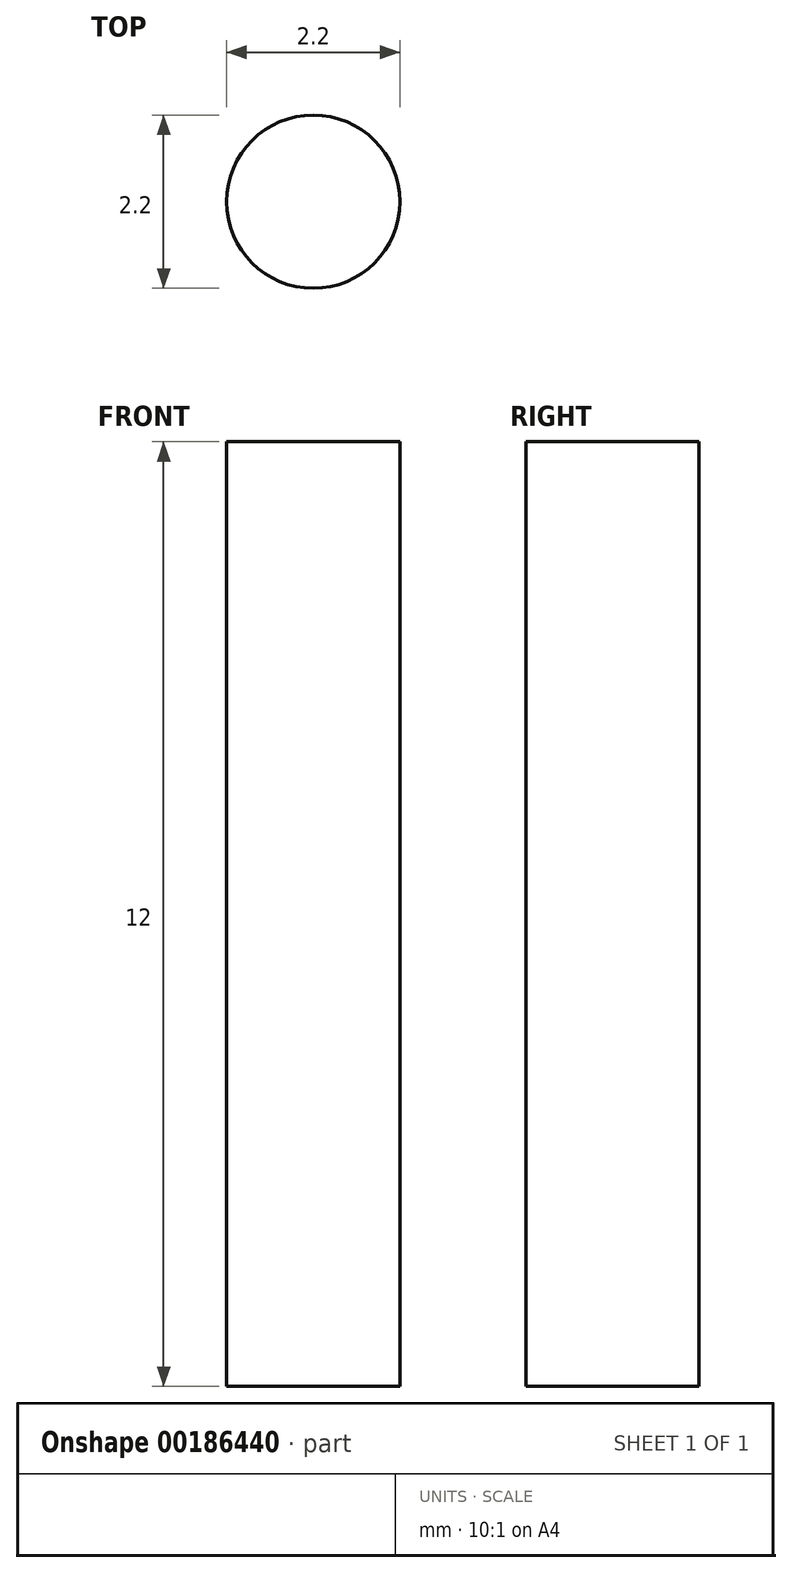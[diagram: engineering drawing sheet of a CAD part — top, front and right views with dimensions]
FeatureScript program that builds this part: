
annotation { "Feature Type Name" : "Feature", "Feature Type Description" : "" }
export const myFeature = defineFeature(function(context is Context, id is Id, definition is map)
    precondition{}
    {
        {
            var Q0;
            Q0=qCreatedBy(makeId("Top.planeOp"),FACE);
            var sketch = newSketch(context, id + "F0", { "sketchPlane" : qUnion([Q0])});
            skCircle(sketch, "E0", {"center": v(0, 0) * mm, "radius": 1.1 * mm});
            skSolve(sketch);
        }
        {
            var Q0;
            Q0 = qSketchRegion(id + "F0", true);
            extrude(context, id + "F1", {"entities" : qUnion([Q0]), "depth" : 12 * mm});
        }
    });
